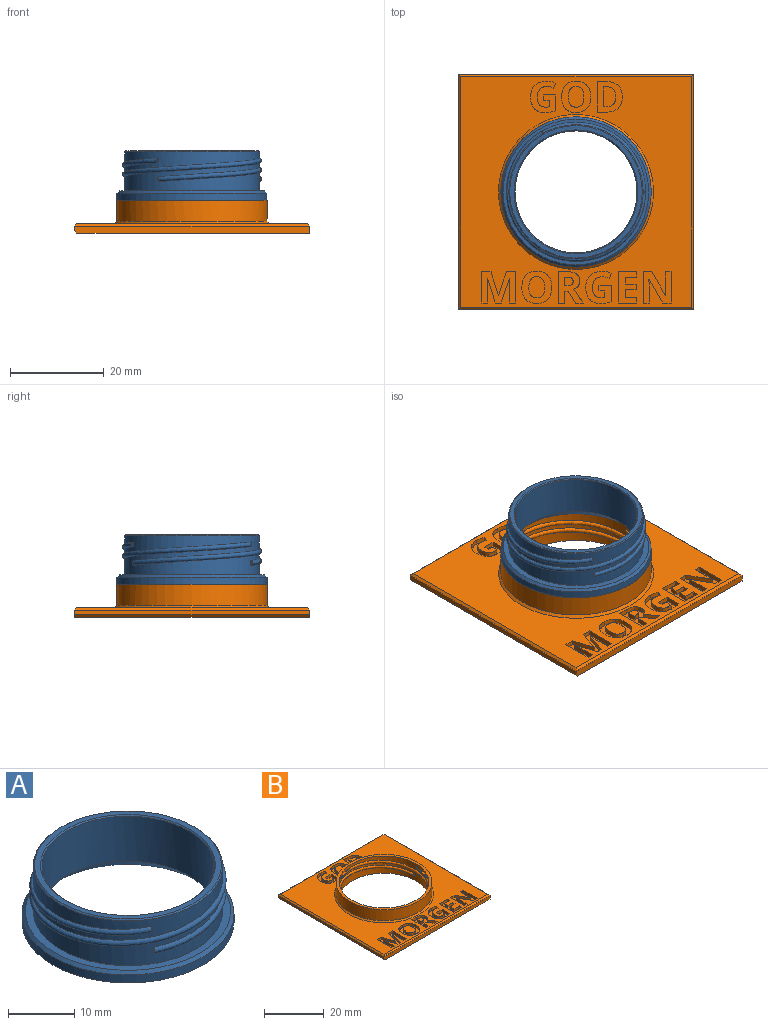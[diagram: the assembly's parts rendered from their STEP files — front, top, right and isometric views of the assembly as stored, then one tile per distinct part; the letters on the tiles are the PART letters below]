
ASSEMBLY  parts=2 mates=1
PART A: 25 faces, bbox 32x35.3x10.5 mm
  f0: plane 0.59x0.26mm, normal (0.87,0.5,0), area 0.1mm2, adj f8,f17
  f1: plane 0.59x0.26mm, normal (-0.87,0.5,0), area 0.1mm2, adj f8,f19
  f2: plane 0.59x0.3mm, normal (0,-1,0), area 0.1mm2, adj f8,f18
  f3: bspline ~30.92x30.6mm, area 95.5mm2, adj f8,f14,f18
  f4: plane 0.61x0.31mm, normal (0,1,0), area 0.1mm2, adj f8,f13
  f5: plane 0.61x0.27mm, normal (-0.87,-0.5,0), area 0.1mm2, adj f8,f12
  f6: plane 0.61x0.27mm, normal (0.87,-0.5,0), area 0.1mm2, adj f8,f14
  f7: cylinder r=13mm len=26mm, axis (0,0,-1), area 678mm2, adj f15,f23
  f8: cylinder r=14.3mm len=28.6mm, axis (0,0,-1), area 566.3mm2, adj f0,f1,f2,f3,f4,f5,f6,f9
  f9: bspline ~29.57x27.47mm, area 95.6mm2, adj f8,f13,f17
  f10: bspline ~35.33x22.95mm, area 95.5mm2, adj f8,f12,f19
  f11: plane 28.2x28.2mm, normal (0,0,1), area 77.2mm2, adj f15,f16
  f12: bspline ~1.1x0.58mm, area 0.4mm2, adj f5,f8,f10
  f13: bspline ~1.1x0.58mm, area 0.4mm2, adj f4,f8,f9
  f14: bspline ~1.1x0.51mm, area 0.4mm2, adj f3,f6,f8
  f15: cone r=13mm half-angle=45deg, axis (0,0,1), area 23.3mm2, adj f7,f11
  f16: cone r=14.1mm half-angle=45deg, axis (0,0,-1), area 25.2mm2, adj f8,f11
  f17: bspline ~1.1x0.51mm, area 0.4mm2, adj f0,f8,f9
  f18: bspline ~1.1x0.58mm, area 0.4mm2, adj f2,f3,f8
  f19: bspline ~1.1x0.59mm, area 0.4mm2, adj f1,f8,f10
  f20: cylinder r=16mm len=32mm, axis (0,0,1), area 150.8mm2, adj f21,f24
  f21: plane 32x32mm, normal (0,0,-1), area 97.4mm2, adj f20,f23
  f22: plane 31x31mm, normal (0,0,1), area 112.3mm2, adj f8,f24
  f23: cone r=15mm half-angle=45deg, axis (0,0,-1), area 248.8mm2, adj f7,f21
  f24: cone r=16mm half-angle=45deg, axis (0,0,-1), area 70mm2, adj f20,f22
PART B: 191 faces, bbox 50.1x50.1x7.1 mm
  f0: plane 49x49mm, normal (0,0,1), area 1304.1mm2, adj f31,f32,f33,f34,f35,f36,f37,f38
  f1: plane 5.54x5.5mm, normal (0,0,-1), area 2.9mm2, adj f9,f12,f13,f20
  f2: plane 7.5x2.04mm, normal (0,0,-1), area 2.9mm2, adj f9,f14,f15,f19
  f3: plane 7.55x2.21mm, normal (0,0,1), area 2.9mm2, adj f8,f9,f17,f23
  f4: plane 5.54x5.5mm, normal (0,0,1), area 2.9mm2, adj f6,f9,f15,f21
  f5: plane 7.55x2.09mm, normal (0,0,1), area 2.9mm2, adj f7,f9,f12,f22
  f6: plane 0.17x0.13mm, normal (0.87,-0.5,0), area 0mm2, adj f4,f9,f21
  f7: plane 0.22x0.2mm, normal (0,1,0), area 0mm2, adj f5,f9,f22
  f8: plane 0.22x0.17mm, normal (-0.87,-0.5,0), area 0mm2, adj f3,f9,f23
  f9: cylinder r=15mm len=30mm, axis (0,0,-1), area 484.3mm2, adj f1,f2,f3,f4,f5,f6,f7,f8
  f10: cylinder r=16mm len=32mm, axis (0,0,-1), area 452.4mm2, adj f24,f31
  f11: plane 7.5x2.1mm, normal (0,0,-1), area 2.9mm2, adj f9,f16,f17,f18
  f12: bspline ~30.31x30mm, area 87.2mm2, adj f1,f5,f9,f20,f22
  f13: plane 0.17x0.13mm, normal (0.87,0.5,0), area 0mm2, adj f1,f9,f20
  f14: plane 0.17x0.15mm, normal (0,-1,0), area 0mm2, adj f2,f9,f19
  f15: bspline ~30.31x30mm, area 87.2mm2, adj f2,f4,f9,f19,f21
  f16: plane 0.17x0.13mm, normal (-0.87,0.5,0), area 0mm2, adj f9,f11,f18
  f17: bspline ~29.92x21.58mm, area 87.3mm2, adj f3,f9,f11,f18,f23
  f18: bspline ~1.13x0.83mm, area 0.6mm2, adj f9,f11,f16,f17
  f19: bspline ~1.02x0.83mm, area 0.6mm2, adj f2,f9,f14,f15
  f20: bspline ~1.02x0.96mm, area 0.6mm2, adj f1,f9,f12,f13
  f21: bspline ~1.02x0.96mm, area 0.6mm2, adj f4,f6,f9,f15
  f22: bspline ~0.99x0.7mm, area 0.6mm2, adj f5,f7,f9,f12
  f23: bspline ~1.12x0.72mm, area 0.6mm2, adj f3,f8,f9,f17
  f24: plane 32x32mm, normal (0,0,1), area 97.4mm2, adj f9,f10
  f25: plane 50x1.5mm, normal (0,1,0), area 74.9mm2, adj f26,f28,f29,f30,f33
  f26: plane 50x1.5mm, normal (1,0,0), area 75mm2, adj f25,f27,f29,f32
  f27: plane 50x1.5mm, normal (0,-1,0), area 74.9mm2, adj f26,f28,f29,f30,f34
  f28: plane 50x1mm, normal (-1,0,0), area 50mm2, adj f25,f27,f30,f35
  f29: plane 50x49.5mm, normal (0,0,-1), area 1768.1mm2, adj f9,f25,f26,f27,f30
  f30: plane 50x0.5mm, normal (-0.71,0,-0.71), area 35.4mm2, adj f25,f27,f28,f29
  f31: cone r=16.5mm half-angle=45deg, axis (0,0,-1), area 72.2mm2, adj f0,f10
  f32: plane 50x0.5mm, normal (0.71,0,0.71), area 35mm2, adj f0,f26,f33,f34
  f33: plane 50x0.5mm, normal (0,0.71,0.71), area 35mm2, adj f0,f25,f32,f35
  f34: plane 50x0.5mm, normal (0,-0.71,0.71), area 35mm2, adj f0,f27,f32,f35
  f35: plane 50x0.5mm, normal (-0.71,0,0.71), area 35mm2, adj f0,f28,f33,f34
  f36: plane 2.58x1mm, normal (0,-1,0), area 2.6mm2, adj f0,f37,f54,f55
  f37: plane 1.15x1mm, normal (1,0,0), area 1.2mm2, adj f0,f36,f38,f55
  f38: plane 1.23x1mm, normal (0,1,0), area 1.2mm2, adj f0,f37,f39,f55
  f39: plane 1.36x1mm, normal (1,0,0), area 1.4mm2, adj f0,f38,f40,f55
  f40: extruded ~1x0.88mm, area 0.9mm2, adj f0,f39,f41,f55
  f41: extruded ~1.26x1mm, area 1.4mm2, adj f0,f40,f42,f55
  f42: extruded ~1.62x1mm, area 1.7mm2, adj f0,f41,f43,f55
  f43: extruded ~1.62x1mm, area 1.7mm2, adj f0,f42,f44,f55
  f44: extruded ~1.43x1mm, area 1.6mm2, adj f0,f43,f45,f55
  f45: extruded ~1.48x1mm, area 1.5mm2, adj f0,f44,f46,f55
  f46: plane 1.1x1mm, normal (-0.92,0.38,0), area 1.2mm2, adj f0,f45,f47,f55
  f47: extruded ~1.93x1mm, area 2mm2, adj f0,f46,f48,f55
  f48: extruded ~2.5x1mm, area 2.7mm2, adj f0,f47,f49,f55
  f49: extruded ~2.46x1mm, area 2.7mm2, adj f0,f48,f50,f55
  f50: extruded ~2.49x1mm, area 2.7mm2, adj f0,f49,f51,f55
  f51: extruded ~2.25x1mm, area 2.5mm2, adj f0,f50,f52,f55
  f52: extruded ~1.13x1mm, area 1.1mm2, adj f0,f51,f53,f55
  f53: extruded ~1.18x1mm, area 1.2mm2, adj f0,f52,f54,f55
  f54: plane 3.38x1mm, normal (-1,0,0), area 3.4mm2, adj f0,f36,f53,f55
  f55: plane 6.69x5.34mm, normal (0,0,1), area 20.7mm2, adj f36,f37,f38,f39,f40,f41,f42,f43
  f56: plane 2.56x1mm, normal (-1,0,0), area 2.6mm2, adj f0,f57,f74,f75
  f57: plane 1x0.75mm, normal (0,1,0), area 0.8mm2, adj f0,f56,f58,f75
  f58: plane 2.56x1.59mm, normal (0.85,0.53,0), area 3mm2, adj f0,f57,f59,f75
  f59: plane 1.57x1mm, normal (0,1,0), area 1.6mm2, adj f0,f58,f60,f75
  f60: extruded ~2.9x1.96mm, area 3.5mm2, adj f0,f59,f61,f75
  f61: extruded ~1x0.92mm, area 1.2mm2, adj f0,f60,f62,f75
  f62: extruded ~1.05x1mm, area 1.1mm2, adj f0,f61,f63,f75
  f63: extruded ~1.5x1mm, area 1.7mm2, adj f0,f62,f64,f75
  f64: extruded ~2.01x1mm, area 2.1mm2, adj f0,f63,f65,f75
  f65: plane 1.94x1mm, normal (0,-1,0), area 1.9mm2, adj f0,f64,f66,f75
  f66: plane 6.66x1mm, normal (1,0,0), area 6.7mm2, adj f0,f65,f74,f75
  f67: plane 1x0.46mm, normal (0,-1,0), area 0.5mm2, adj f68,f73,f75,f76
  f68: plane 1.8x1mm, normal (-1,0,0), area 1.8mm2, adj f67,f69,f75,f76
  f69: plane 1x0.43mm, normal (0,1,0), area 0.4mm2, adj f68,f70,f75,f76
  f70: extruded ~1.01x1mm, area 1mm2, adj f69,f71,f75,f76
  f71: extruded ~1x0.67mm, area 0.8mm2, adj f70,f72,f75,f76
  f72: extruded ~1x0.7mm, area 0.8mm2, adj f71,f73,f75,f76
  f73: extruded ~1x0.99mm, area 1mm2, adj f67,f72,f75,f76
  f74: plane 1.41x1mm, normal (0,1,0), area 1.4mm2, adj f0,f56,f66,f75
  f75: plane 6.66x5.32mm, normal (0,0,1), area 21.7mm2, adj f56,f57,f58,f59,f60,f61,f62,f63
  f76: plane 1.8x1.76mm, normal (0,0,1), area 2.8mm2, adj f67,f68,f69,f70,f71,f72,f73
  f77: extruded ~1.68x1mm, area 1.8mm2, adj f78,f90,f91,f188
  f78: extruded ~1.68x1mm, area 1.8mm2, adj f77,f79,f91,f188
  f79: extruded ~1.27x1mm, area 1.4mm2, adj f78,f80,f91,f188
  f80: extruded ~2.25x1.68mm, area 3.2mm2, adj f79,f81,f91,f188
  f81: extruded ~2.25x1.69mm, area 3.2mm2, adj f80,f90,f91,f188
  f82: extruded ~2.54x1mm, area 2.7mm2, adj f0,f83,f89,f91
  f83: extruded ~2.54x1mm, area 2.7mm2, adj f0,f82,f84,f91
  f84: extruded ~2.35x1mm, area 2.6mm2, adj f0,f83,f85,f91
  f85: extruded ~2.36x1mm, area 2.6mm2, adj f0,f84,f86,f91
  f86: extruded ~2.54x1mm, area 2.7mm2, adj f0,f85,f87,f91
  f87: extruded ~2.55x1mm, area 2.7mm2, adj f0,f86,f88,f91
  f88: extruded ~2.35x1mm, area 2.6mm2, adj f0,f87,f89,f91
  f89: extruded ~2.35x1mm, area 2.6mm2, adj f0,f82,f88,f91
  f90: extruded ~1.27x1mm, area 1.4mm2, adj f77,f81,f91,f188
  f91: plane 6.86x6.34mm, normal (0,0,1), area 23.3mm2, adj f77,f78,f79,f80,f81,f82,f83,f84
  f92: extruded ~2.1x1.85mm, area 3.2mm2, adj f93,f103,f104,f189
  f93: extruded ~2.14x2mm, area 3.4mm2, adj f92,f94,f104,f189
  f94: plane 1x0.59mm, normal (0,-1,0), area 0.6mm2, adj f93,f95,f104,f189
  f95: plane 4.24x1mm, normal (-1,0,0), area 4.2mm2, adj f94,f103,f104,f189
  f96: extruded ~2.46x1mm, area 2.7mm2, adj f0,f97,f102,f104
  f97: extruded ~2.35x1mm, area 2.6mm2, adj f0,f96,f98,f104
  f98: extruded ~2.48x1mm, area 2.7mm2, adj f0,f97,f99,f104
  f99: plane 2.04x1mm, normal (0,-1,0), area 2mm2, adj f0,f98,f100,f104
  f100: plane 6.51x1mm, normal (1,0,0), area 6.5mm2, adj f0,f99,f101,f104
  f101: plane 1.84x1mm, normal (0,1,0), area 1.8mm2, adj f0,f100,f102,f104
  f102: extruded ~2.64x1mm, area 2.8mm2, adj f0,f96,f101,f104
  f103: plane 1x0.73mm, normal (0,1,0), area 0.7mm2, adj f92,f95,f104,f189
  f104: plane 6.51x5.4mm, normal (0,0,1), area 21.6mm2, adj f92,f93,f94,f95,f96,f97,f98,f99
  f105: extruded ~1.64x1mm, area 1.7mm2, adj f106,f118,f119,f190
  f106: extruded ~1.64x1mm, area 1.7mm2, adj f105,f107,f119,f190
  f107: extruded ~1.24x1mm, area 1.4mm2, adj f106,f108,f119,f190
  f108: extruded ~2.2x1.64mm, area 3.1mm2, adj f107,f109,f119,f190
  f109: extruded ~2.2x1.65mm, area 3.1mm2, adj f108,f118,f119,f190
  f110: extruded ~2.49x1mm, area 2.7mm2, adj f0,f111,f117,f119
  f111: extruded ~2.49x1mm, area 2.7mm2, adj f0,f110,f112,f119
  f112: extruded ~2.3x1mm, area 2.5mm2, adj f0,f111,f113,f119
  f113: extruded ~2.3x1mm, area 2.5mm2, adj f0,f112,f114,f119
  f114: extruded ~2.48x1mm, area 2.7mm2, adj f0,f113,f115,f119
  f115: extruded ~2.49x1mm, area 2.7mm2, adj f0,f114,f116,f119
  f116: extruded ~2.3x1mm, area 2.5mm2, adj f0,f115,f117,f119
  f117: extruded ~2.3x1mm, area 2.5mm2, adj f0,f110,f116,f119
  f118: extruded ~1.24x1mm, area 1.4mm2, adj f105,f109,f119,f190
  f119: plane 6.7x6.2mm, normal (0,0,1), area 22.2mm2, adj f105,f106,f107,f108,f109,f110,f111,f112
  f120: plane 1.8x1mm, normal (0,1,0), area 1.8mm2, adj f0,f121,f133,f134
  f121: plane 6.66x1mm, normal (-1,0,0), area 6.7mm2, adj f0,f120,f122,f134
  f122: plane 1.27x1mm, normal (0,-1,0), area 1.3mm2, adj f0,f121,f123,f134
  f123: plane 3.15x1mm, normal (1,0,0), area 3.2mm2, adj f0,f122,f124,f134
  f124: extruded ~1.84x1mm, area 1.8mm2, adj f0,f123,f125,f134
  f125: plane 1x0.03mm, normal (0,-1,0), area 0mm2, adj f0,f124,f126,f134
  f126: plane 4.99x2.89mm, normal (-0.87,-0.5,0), area 5.8mm2, adj f0,f125,f127,f134
  f127: plane 1.78x1mm, normal (0,-1,0), area 1.8mm2, adj f0,f126,f128,f134
  f128: plane 6.66x1mm, normal (1,0,0), area 6.7mm2, adj f0,f127,f129,f134
  f129: plane 1.26x1mm, normal (0,1,0), area 1.3mm2, adj f0,f128,f130,f134
  f130: plane 3.14x1mm, normal (-1,0,0), area 3.1mm2, adj f0,f129,f131,f134
  f131: extruded ~1.9x1mm, area 1.9mm2, adj f0,f130,f132,f134
  f132: plane 1x0.04mm, normal (0,1,0), area 0mm2, adj f0,f131,f133,f134
  f133: plane 5.04x2.9mm, normal (0.87,0.5,0), area 5.8mm2, adj f0,f120,f132,f134
  f134: plane 6.66x5.91mm, normal (0,0,1), area 25.2mm2, adj f120,f121,f122,f123,f124,f125,f126,f127
  f135: plane 3.84x1mm, normal (0,1,0), area 3.8mm2, adj f0,f136,f146,f147
  f136: plane 1.17x1mm, normal (-1,0,0), area 1.2mm2, adj f0,f135,f137,f147
  f137: plane 2.42x1mm, normal (0,-1,0), area 2.4mm2, adj f0,f136,f138,f147
  f138: plane 1.72x1mm, normal (-1,0,0), area 1.7mm2, adj f0,f137,f139,f147
  f139: plane 2.26x1mm, normal (0,1,0), area 2.3mm2, adj f0,f138,f140,f147
  f140: plane 1.16x1mm, normal (-1,0,0), area 1.2mm2, adj f0,f139,f141,f147
  f141: plane 2.26x1mm, normal (0,-1,0), area 2.3mm2, adj f0,f140,f142,f147
  f142: plane 1.46x1mm, normal (-1,0,0), area 1.5mm2, adj f0,f141,f143,f147
  f143: plane 2.42x1mm, normal (0,1,0), area 2.4mm2, adj f0,f142,f144,f147
  f144: plane 1.16x1mm, normal (-1,0,0), area 1.2mm2, adj f0,f143,f145,f147
  f145: plane 3.84x1mm, normal (0,-1,0), area 3.8mm2, adj f0,f144,f146,f147
  f146: plane 6.66x1mm, normal (1,0,0), area 6.7mm2, adj f0,f135,f145,f147
  f147: plane 6.66x3.84mm, normal (0,0,1), area 17.7mm2, adj f135,f136,f137,f138,f139,f140,f141,f142
  f148: plane 2.64x1mm, normal (0,-1,0), area 2.6mm2, adj f0,f149,f166,f167
  f149: plane 1.18x1mm, normal (1,0,0), area 1.2mm2, adj f0,f148,f150,f167
  f150: plane 1.26x1mm, normal (0,1,0), area 1.3mm2, adj f0,f149,f151,f167
  f151: plane 1.39x1mm, normal (1,0,0), area 1.4mm2, adj f0,f150,f152,f167
  f152: extruded ~1x0.9mm, area 0.9mm2, adj f0,f151,f153,f167
  f153: extruded ~1.29x1mm, area 1.5mm2, adj f0,f152,f154,f167
  f154: extruded ~1.66x1mm, area 1.7mm2, adj f0,f153,f155,f167
  f155: extruded ~1.65x1mm, area 1.8mm2, adj f0,f154,f156,f167
  f156: extruded ~1.47x1mm, area 1.6mm2, adj f0,f155,f157,f167
  f157: extruded ~1.52x1mm, area 1.6mm2, adj f0,f156,f158,f167
  f158: plane 1.13x1mm, normal (-0.92,0.38,0), area 1.2mm2, adj f0,f157,f159,f167
  f159: extruded ~1.98x1mm, area 2mm2, adj f0,f158,f160,f167
  f160: extruded ~2.56x1mm, area 2.8mm2, adj f0,f159,f161,f167
  f161: extruded ~2.52x1mm, area 2.8mm2, adj f0,f160,f162,f167
  f162: extruded ~2.55x1mm, area 2.7mm2, adj f0,f161,f163,f167
  f163: extruded ~2.3x1mm, area 2.5mm2, adj f0,f162,f164,f167
  f164: extruded ~1.16x1mm, area 1.2mm2, adj f0,f163,f165,f167
  f165: extruded ~1.21x1mm, area 1.2mm2, adj f0,f164,f166,f167
  f166: plane 3.46x1mm, normal (-1,0,0), area 3.5mm2, adj f0,f148,f165,f167
  f167: plane 6.85x5.47mm, normal (0,0,1), area 21.6mm2, adj f148,f149,f150,f151,f152,f153,f154,f155
  f168: plane 5.23x1.6mm, normal (0.96,0.29,0), area 5.5mm2, adj f0,f169,f186,f187
  f169: plane 1.3x1mm, normal (0,1,0), area 1.3mm2, adj f0,f168,f170,f187
  f170: plane 5.22x1.72mm, normal (-0.95,0.31,0), area 5.5mm2, adj f0,f169,f171,f187
  f171: plane 1x0.04mm, normal (0,1,0), area 0mm2, adj f0,f170,f172,f187
  f172: extruded ~1.55x1mm, area 1.6mm2, adj f0,f171,f173,f187
  f173: extruded ~1x0.52mm, area 0.5mm2, adj f0,f172,f174,f187
  f174: plane 3.15x1mm, normal (1,0,0), area 3.2mm2, adj f0,f173,f175,f187
  f175: plane 1.32x1mm, normal (0,1,0), area 1.3mm2, adj f0,f174,f176,f187
  f176: plane 6.66x1mm, normal (-1,0,0), area 6.7mm2, adj f0,f175,f177,f187
  f177: plane 1.92x1mm, normal (0,-1,0), area 1.9mm2, adj f0,f176,f178,f187
  f178: plane 5.1x1.67mm, normal (0.95,-0.31,0), area 5.4mm2, adj f0,f177,f179,f187
  f179: plane 1x0.03mm, normal (0,-1,0), area 0mm2, adj f0,f178,f180,f187
  f180: plane 5.1x1.58mm, normal (-0.96,-0.3,0), area 5.3mm2, adj f0,f179,f181,f187
  f181: plane 1.92x1mm, normal (0,-1,0), area 1.9mm2, adj f0,f180,f182,f187
  f182: plane 6.66x1mm, normal (1,0,0), area 6.7mm2, adj f0,f181,f183,f187
  f183: plane 1.26x1mm, normal (0,1,0), area 1.3mm2, adj f0,f182,f184,f187
  f184: plane 3.1x1mm, normal (-1,0,0), area 3.1mm2, adj f0,f183,f185,f187
  f185: extruded ~2.13x1mm, area 2.1mm2, adj f0,f184,f186,f187
  f186: plane 1x0.04mm, normal (0,1,0), area 0mm2, adj f0,f168,f185,f187
  f187: plane 7.12x6.66mm, normal (0,0,1), area 30.6mm2, adj f168,f169,f170,f171,f172,f173,f174,f175
  f188: plane 4.5x3.38mm, normal (0,0,1), area 12.7mm2, adj f77,f78,f79,f80,f81,f90
  f189: plane 4.24x2.59mm, normal (0,0,1), area 9.6mm2, adj f92,f93,f94,f95,f103
  f190: plane 4.4x3.3mm, normal (0,0,1), area 12.1mm2, adj f105,f106,f107,f108,f109,f118
PLACE A t=(-0.23,0.26,6.38)mm
PLACE B t=(-0.23,0.26,-3.12)mm fixed
MATE fastened A.f7 <-> B.f9  axis (0,0,-1) through (-0.23,0.26,1.88)mm
